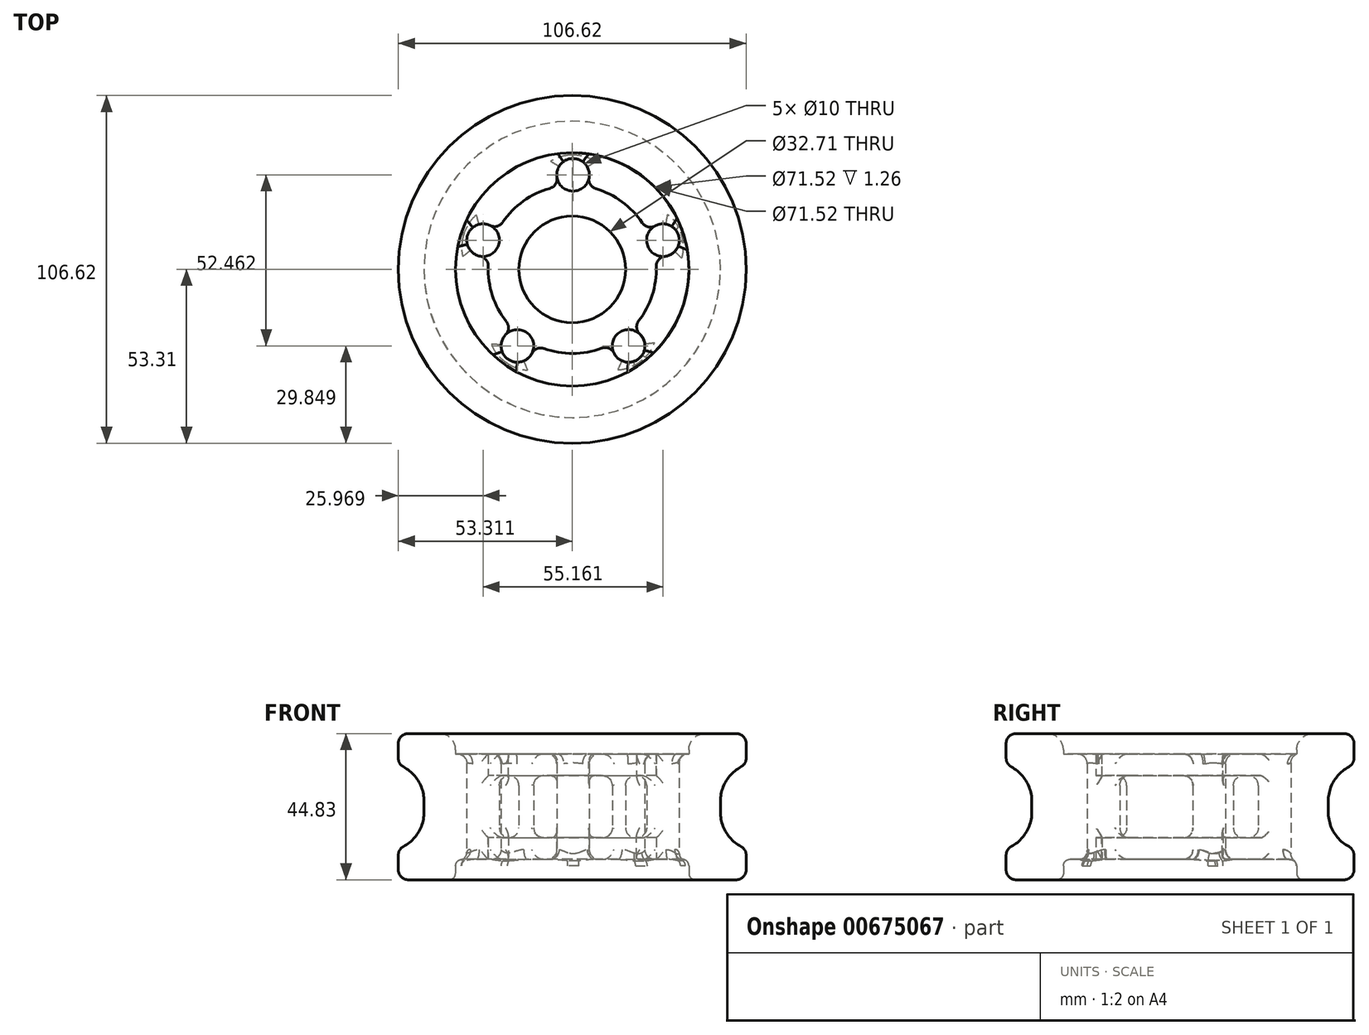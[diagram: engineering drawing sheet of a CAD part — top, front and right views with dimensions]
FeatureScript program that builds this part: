
annotation { "Feature Type Name" : "Feature", "Feature Type Description" : "" }
export const myFeature = defineFeature(function(context is Context, id is Id, definition is map)
    precondition{}
    {
        {
            var Q0;
            Q0=qCreatedBy(makeId("Front.planeOp"),FACE);
            var sketch = newSketch(context, id + "F0", { "sketchPlane" : qUnion([Q0])});
            skLineSegment(sketch, "E0", {"start": v(-62.64, 22.41) * mm, "end": v(-0.24, 22.41) * mm, "construction": true});
            skLineSegment(sketch, "E1", {"start": v(-16.6, 22.41) * mm, "end": v(-16.6, 31.9) * mm});
            skLineSegment(sketch, "E2", {"start": v(-16.1, 31.9) * mm, "end": v(-26, 31.9) * mm});
            skLineSegment(sketch, "E3", {"start": v(-26, 31.9) * mm, "end": v(-26, 38.57) * mm});
            skLineSegment(sketch, "E4", {"start": v(-26, 38.57) * mm, "end": v(-36, 38.57) * mm});
            skLineSegment(sketch, "E5", {"start": v(-36, 38.57) * mm, "end": v(-36, 44.83) * mm});
            skLineSegment(sketch, "E6", {"start": v(-36, 44.83) * mm, "end": v(-53.55, 44.83) * mm});
            skLineSegment(sketch, "E7", {"start": v(-53.55, 44.83) * mm, "end": v(-53.55, 35.34) * mm});
            skLineSegment(sketch, "E8", {"start": v(-53.55, 35.34) * mm, "end": v(-45.67, 35.34) * mm});
            skLineSegment(sketch, "E9", {"start": v(-45.67, 35.34) * mm, "end": v(-45.67, 22.41) * mm});
            skLineSegment(sketch, "E10.MirrorCS", {"start": v(-16.6, 22.41) * mm, "end": v(-16.6, 12.92) * mm});
            skLineSegment(sketch, "E11.MirrorCS", {"start": v(-16.1, 12.92) * mm, "end": v(-26, 12.92) * mm});
            skLineSegment(sketch, "E12.MirrorCS", {"start": v(-26, 12.92) * mm, "end": v(-26, 6.26) * mm});
            skLineSegment(sketch, "E13.MirrorCS", {"start": v(-26, 6.26) * mm, "end": v(-36, 6.26) * mm});
            skLineSegment(sketch, "E14.MirrorCS", {"start": v(-36, 6.26) * mm, "end": v(-36, 0) * mm});
            skLineSegment(sketch, "E15.MirrorCS", {"start": v(-36, 0) * mm, "end": v(-53.55, 0) * mm});
            skLineSegment(sketch, "E16.MirrorCS", {"start": v(-53.55, 0) * mm, "end": v(-53.55, 9.5) * mm});
            skLineSegment(sketch, "E17.MirrorCS", {"start": v(-45.67, 9.5) * mm, "end": v(-45.67, 22.41) * mm});
            skLineSegment(sketch, "E18.MirrorCS", {"start": v(-53.55, 9.5) * mm, "end": v(-45.67, 9.5) * mm});
            skLineSegment(sketch, "E19", {"start": v(-0.24, 22.41) * mm, "end": v(-0.24, 53.92) * mm, "construction": true});
            skLineSegment(sketch, "E20", {"start": v(-36, 0) * mm, "end": v(0, 0) * mm, "construction": true});
            skSolve(sketch);
        }
        {
            var Q0;
            {var subQ1=sQuery(id+"F0.wireOp",EDGE,"E1");Q0=makeQuery(id+"F0.imprint","IMPRINT",FACE,{"disambiguationData":[TD([[makeQuery(id+"F0.imprint","IMPRINT",EDGE,{"derivedFrom":subQ1}),1.0]])]});}
            var Q1;
            Q1=sQuery(id+"F0.wireOp",EDGE,"E19");
            revolve(context, id + "F1", {"entities" : qUnion([Q0]), "axis" : qUnion([Q1]), "revolveType" : RevolveType.FULL});
        }
        {
            var Q0;
            Q0=makeQuery(id+"F1.opRevolve","SWEPT_FACE",FACE,{"disambiguationData":[OSD([sQuery(id+"F0.wireOp",EDGE,"E9"),sQuery(id+"F0.wireOp",EDGE,"E17.MirrorCS")])]});
            fillet(context, id + "F2", {"entities" : qUnion([Q0]), "radius" : 12 * mm, "tangentPropagation" : true, "allowEdgeOverflow" : false});
        }
        {
            var Q0;
            Q0=makeQuery(id+"F1.opRevolve","SWEPT_FACE",FACE,{"disambiguationData":[OSD([sQuery(id+"F0.wireOp",EDGE,"E7")])]});
            fillet(context, id + "F3", {"entities" : qUnion([Q0]), "radius" : 3 * mm, "tangentPropagation" : true, "allowEdgeOverflow" : false});
        }
        {
            var Q0;
            Q0=makeQuery(id+"F1.opRevolve","SWEPT_FACE",FACE,{"disambiguationData":[OSD([sQuery(id+"F0.wireOp",EDGE,"E16.MirrorCS")])]});
            fillet(context, id + "F4", {"entities" : qUnion([Q0]), "radius" : 3 * mm, "tangentPropagation" : true, "allowEdgeOverflow" : false});
        }
        {
            var Q0;
            Q0=qCreatedBy(makeId("Top.planeOp"),FACE);
            var sketch = newSketch(context, id + "F5", { "sketchPlane" : qUnion([Q0])});
            skCircle(sketch, "E21", {"center": v(0, 0) * mm, "radius": 34 * mm, "construction": true});
            skCircle(sketch, "E22", {"center": v(0, 0) * mm, "radius": 24 * mm, "construction": true});
            skLineSegment(sketch, "E23", {"start": v(0, 24) * mm, "end": v(0, 34) * mm, "construction": true});
            skCircle(sketch, "E24", {"center": v(0, 29) * mm, "radius": 5 * mm});
            skCircle(sketch, "E25.1.0", {"center": v(-27.58, 8.96) * mm, "radius": 5 * mm});
            skCircle(sketch, "E25.2.0", {"center": v(-17.05, -23.46) * mm, "radius": 5 * mm});
            skCircle(sketch, "E25.3.0", {"center": v(17.05, -23.46) * mm, "radius": 5 * mm});
            skCircle(sketch, "E25.4.0", {"center": v(27.58, 8.96) * mm, "radius": 5 * mm});
            skSolve(sketch);
        }
        {
            var Q0;
            Q0 = qSketchRegion(id + "F5", true);
            extrude(context, id + "F6", {"entities" : qUnion([Q0]), "operationType" : NewBodyOperationType.REMOVE, "depth" : 82.7 * mm, "offsetDistance" : 25 * mm});
        }
        {
            var Q0;
            Q0=makeQuery(id+"F1.opRevolve","SWEPT_EDGE",EDGE,{"disambiguationData":[OSD([sQuery(id+"F0.wireOp",EDGE,"E5"),sQuery(id+"F0.wireOp",EDGE,"E6")])]});
            fillet(context, id + "F7", {"entities" : qUnion([Q0]), "radius" : 5 * mm, "tangentPropagation" : true, "allowEdgeOverflow" : false});
        }
        {
            var Q0;
            Q0=makeQuery(id+"F1.opRevolve","SWEPT_FACE",FACE,{"disambiguationData":[OSD([sQuery(id+"F0.wireOp",EDGE,"E14.MirrorCS")])]});
            fillet(context, id + "F8", {"entities" : qUnion([Q0]), "radius" : 2 * mm, "tangentPropagation" : true, "allowEdgeOverflow" : false});
        }
        {
            var Q0;
            Q0=makeQuery(id+"F6.boolean.opBoolean","COPY",FACE,{"derivedFrom":makeQuery(id+"F6.opExtrude","SWEPT_FACE",FACE,{"disambiguationData":[OSD([sQuery(id+"F5.wireOp",EDGE,"E25.3.0")])]})});
            fillet(context, id + "F9", {"entities" : qUnion([Q0]), "radius" : 3 * mm, "tangentPropagation" : true, "allowEdgeOverflow" : false});
        }
        {
            var Q0;
            Q0=makeQuery(id+"F6.boolean.opBoolean","COPY",FACE,{"derivedFrom":makeQuery(id+"F6.opExtrude","SWEPT_FACE",FACE,{"disambiguationData":[OSD([sQuery(id+"F5.wireOp",EDGE,"E25.2.0")])]})});
            fillet(context, id + "F10", {"entities" : qUnion([Q0]), "radius" : 3 * mm, "tangentPropagation" : true, "allowEdgeOverflow" : false});
        }
        {
            var Q0;
            Q0=makeQuery(id+"F6.boolean.opBoolean","COPY",FACE,{"derivedFrom":makeQuery(id+"F6.opExtrude","SWEPT_FACE",FACE,{"disambiguationData":[OSD([sQuery(id+"F5.wireOp",EDGE,"E25.1.0")])]})});
            fillet(context, id + "F11", {"entities" : qUnion([Q0]), "radius" : 3 * mm, "tangentPropagation" : true, "allowEdgeOverflow" : false});
        }
        {
            var Q0;
            Q0=makeQuery(id+"F6.boolean.opBoolean","COPY",FACE,{"derivedFrom":makeQuery(id+"F6.opExtrude","SWEPT_FACE",FACE,{"disambiguationData":[OSD([sQuery(id+"F5.wireOp",EDGE,"E24")])]})});
            fillet(context, id + "F12", {"entities" : qUnion([Q0]), "radius" : 3 * mm, "tangentPropagation" : true, "allowEdgeOverflow" : false});
        }
        {
            var Q0;
            Q0=makeQuery(id+"F6.boolean.opBoolean","COPY",FACE,{"derivedFrom":makeQuery(id+"F6.opExtrude","SWEPT_FACE",FACE,{"disambiguationData":[OSD([sQuery(id+"F5.wireOp",EDGE,"E25.4.0")])]})});
            fillet(context, id + "F13", {"entities" : qUnion([Q0]), "radius" : 3 * mm, "tangentPropagation" : true, "allowEdgeOverflow" : false});
        }
        {
            var Q0;
            Q0=makeQuery(id+"F1.opRevolve","SWEPT_FACE",FACE,{"disambiguationData":[OSD([sQuery(id+"F0.wireOp",EDGE,"E1"),sQuery(id+"F0.wireOp",EDGE,"E10.MirrorCS")])]});
            fillet(context, id + "F14", {"entities" : qUnion([Q0]), "radius" : 3 * mm, "tangentPropagation" : true, "allowEdgeOverflow" : false});
        }
    });
